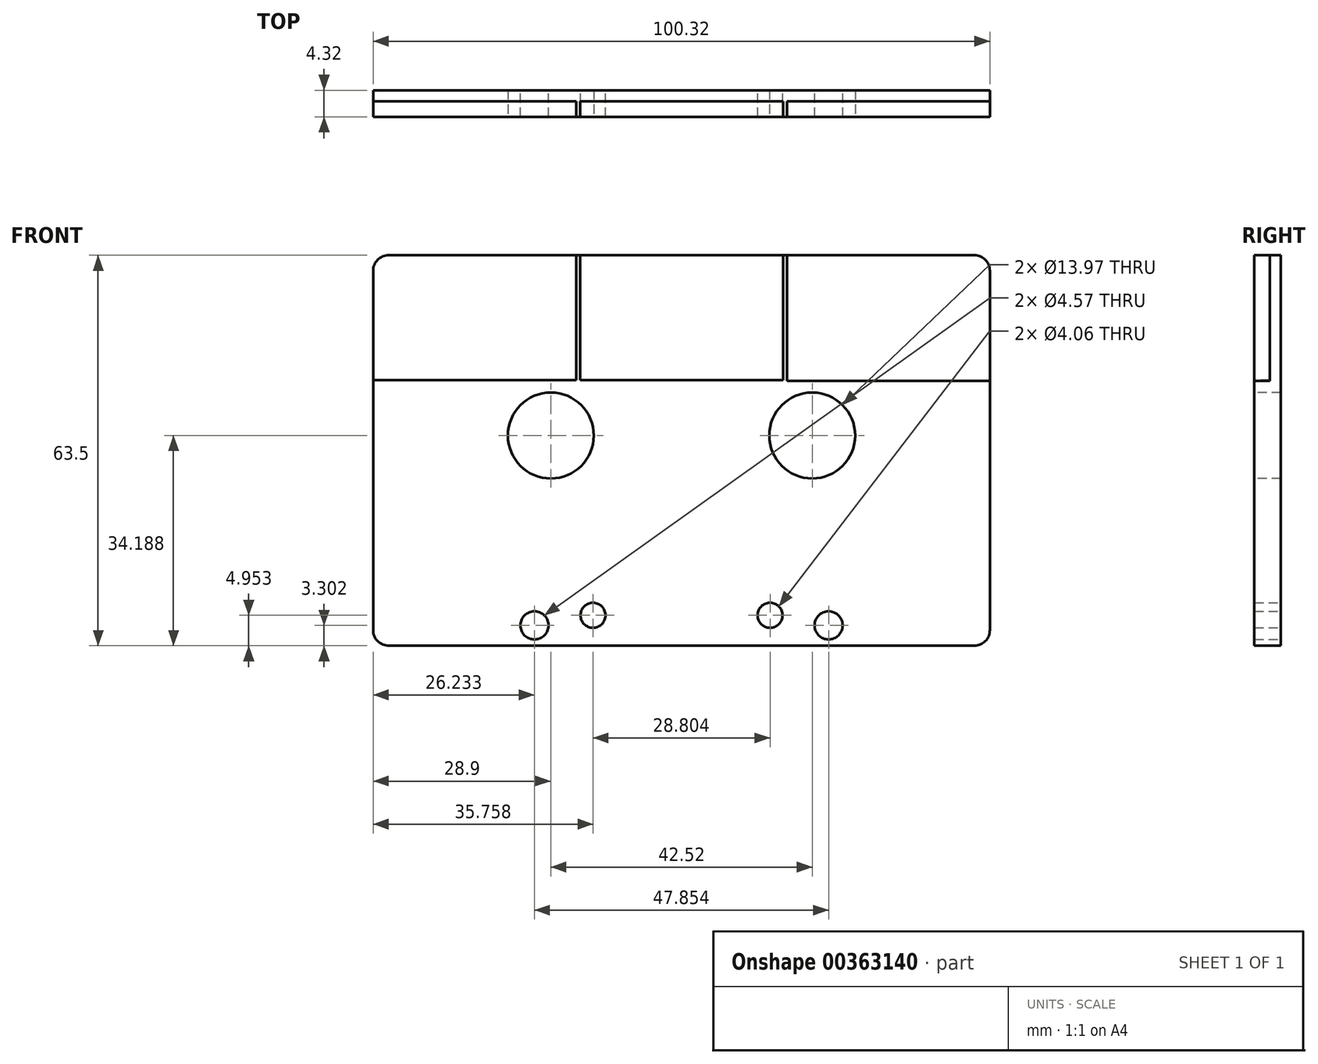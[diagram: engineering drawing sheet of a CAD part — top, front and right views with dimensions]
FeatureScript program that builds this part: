
annotation { "Feature Type Name" : "Feature", "Feature Type Description" : "" }
export const myFeature = defineFeature(function(context is Context, id is Id, definition is map)
    precondition{}
    {
        {
            var Q0;
            Q0=qCreatedBy(makeId("Front.planeOp"),FACE);
            var sketch = newSketch(context, id + "F0", { "sketchPlane" : qUnion([Q0])});
            skLineSegment(sketch, "E0.bottom", {"start": v(-47.63, 0) * mm, "end": v(47.63, 0) * mm});
            skLineSegment(sketch, "E0.top", {"start": v(-47.63, -63.5) * mm, "end": v(47.63, -63.5) * mm});
            skLineSegment(sketch, "E0.left", {"start": v(-50.17, -2.54) * mm, "end": v(-50.17, -60.96) * mm});
            skLineSegment(sketch, "E0.right", {"start": v(50.17, -2.54) * mm, "end": v(50.17, -60.96) * mm});
            skPoint(sketch, "E1.visualSharp", {"position": v(-50.17, 0) * mm});
            skArc(sketch, "E1.filletArc", {"start": v(-47.63, 0) * mm, "mid": v(-49.42, -0.74) * mm, "end": v(-50.17, -2.54) * mm});
            skPoint(sketch, "E2.visualSharp", {"position": v(50.17, 0) * mm});
            skArc(sketch, "E2.filletArc", {"start": v(50.17, -2.54) * mm, "mid": v(49.42, -0.74) * mm, "end": v(47.63, 0) * mm});
            skPoint(sketch, "E3.visualSharp", {"position": v(50.17, -63.5) * mm});
            skArc(sketch, "E3.filletArc", {"start": v(47.63, -63.5) * mm, "mid": v(49.42, -62.76) * mm, "end": v(50.17, -60.96) * mm});
            skPoint(sketch, "E4.visualSharp", {"position": v(-50.17, -63.5) * mm});
            skArc(sketch, "E4.filletArc", {"start": v(-50.16, -60.96) * mm, "mid": v(-49.42, -62.76) * mm, "end": v(-47.63, -63.5) * mm});
            skSolve(sketch);
        }
        {
            var Q0;
            Q0 = qSketchRegion(id + "F0", true);
            extrude(context, id + "F1", {"entities" : qUnion([Q0]), "depth" : 4.32 * mm});
        }
        {
            var Q0;
            Q0=makeQuery(id+"F1.opExtrude","CAP_FACE",FACE,{"disambiguationData":[OSD([sQuery(id+"F0.wireOp",EDGE,"E0.bottom"),sQuery(id+"F0.wireOp",EDGE,"E0.top"),sQuery(id+"F0.wireOp",EDGE,"E0.left"),sQuery(id+"F0.wireOp",EDGE,"E0.right"),sQuery(id+"F0.wireOp",EDGE,"E1.filletArc"),sQuery(id+"F0.wireOp",EDGE,"E2.filletArc"),sQuery(id+"F0.wireOp",EDGE,"E3.filletArc"),sQuery(id+"F0.wireOp",EDGE,"E4.filletArc")])],"isStart":false});
            var sketch = newSketch(context, id + "F2", { "sketchPlane" : qUnion([Q0])});
            skPoint(sketch, "E5", {"position": v(21.26, -29.31) * mm});
            skPoint(sketch, "E6", {"position": v(-21.26, -29.31) * mm});
            skSolve(sketch);
        }
        {
            var Q0;
            Q0=sQuery(id+"F2.wireOp",VERTEX,"E6");
            var Q1;
            Q1=sQuery(id+"F2.wireOp",VERTEX,"E5");
            var Q2;
            Q2=makeQuery(id+"F1.opExtrude","SWEPT_BODY",BODY,{"disambiguationData":[OSD([sQuery(id+"F0.wireOp",EDGE,"E0.bottom"),sQuery(id+"F0.wireOp",EDGE,"E0.top"),sQuery(id+"F0.wireOp",EDGE,"E0.left"),sQuery(id+"F0.wireOp",EDGE,"E0.right"),sQuery(id+"F0.wireOp",EDGE,"E1.filletArc"),sQuery(id+"F0.wireOp",EDGE,"E2.filletArc"),sQuery(id+"F0.wireOp",EDGE,"E3.filletArc"),sQuery(id+"F0.wireOp",EDGE,"E4.filletArc")])]});
            hole(context, id + "F3", {"style" : HoleStyle.SIMPLE, "endStyle" : HoleEndStyle.THROUGH, "holeDiameter" : 13.97 * mm, "isTappedThrough" : true, "tappedDepth" : 12.7 * mm, "tapClearance" : 3, "startFromSketch" : true, "locations" : qUnion([Q0, Q1]), "scope" : qUnion([Q2])});
        }
        {
            var Q0;
            Q0=makeQuery(id+"F1.opExtrude","CAP_FACE",FACE,{"disambiguationData":[OSD([sQuery(id+"F0.wireOp",EDGE,"E0.bottom"),sQuery(id+"F0.wireOp",EDGE,"E0.top"),sQuery(id+"F0.wireOp",EDGE,"E0.left"),sQuery(id+"F0.wireOp",EDGE,"E0.right"),sQuery(id+"F0.wireOp",EDGE,"E1.filletArc"),sQuery(id+"F0.wireOp",EDGE,"E2.filletArc"),sQuery(id+"F0.wireOp",EDGE,"E3.filletArc"),sQuery(id+"F0.wireOp",EDGE,"E4.filletArc")])],"isStart":false});
            var sketch = newSketch(context, id + "F4", { "sketchPlane" : qUnion([Q0])});
            skLineSegment(sketch, "E7.bottom", {"start": v(-16.51, 0) * mm, "end": v(16.5, 0) * mm});
            skLineSegment(sketch, "E7.top", {"start": v(-16.51, -20.32) * mm, "end": v(16.5, -20.32) * mm});
            skLineSegment(sketch, "E7.left", {"start": v(-16.51, 0) * mm, "end": v(-16.51, -20.32) * mm});
            skLineSegment(sketch, "E7.right", {"start": v(16.51, 0) * mm, "end": v(16.51, -20.32) * mm});
            skLineSegment(sketch, "E8.bottom", {"start": v(-50.17, 0) * mm, "end": v(-17.14, 0) * mm});
            skLineSegment(sketch, "E8.top", {"start": v(-50.17, -20.32) * mm, "end": v(-17.14, -20.32) * mm});
            skLineSegment(sketch, "E8.left", {"start": v(-50.17, 0) * mm, "end": v(-50.17, -20.32) * mm});
            skLineSegment(sketch, "E8.right", {"start": v(-17.14, 0) * mm, "end": v(-17.14, -20.32) * mm});
            skLineSegment(sketch, "E9.bottom", {"start": v(17.14, 0) * mm, "end": v(50.17, 0) * mm});
            skLineSegment(sketch, "E9.top", {"start": v(17.14, -20.4) * mm, "end": v(50.17, -20.4) * mm});
            skLineSegment(sketch, "E9.left", {"start": v(17.14, 0) * mm, "end": v(17.14, -20.4) * mm});
            skLineSegment(sketch, "E9.right", {"start": v(50.17, 0) * mm, "end": v(50.17, -20.4) * mm});
            skSolve(sketch);
        }
        {
            var Q0;
            Q0 = qSketchRegion(id + "F4", true);
            extrude(context, id + "F5", {"entities" : qUnion([Q0]), "operationType" : NewBodyOperationType.REMOVE, "oppositeDirection" : true, "depth" : 2.54 * mm});
        }
        {
            var Q0;
            Q0=makeQuery(id+"F1.opExtrude","CAP_FACE",FACE,{"disambiguationData":[OSD([sQuery(id+"F0.wireOp",EDGE,"E0.bottom"),sQuery(id+"F0.wireOp",EDGE,"E0.top"),sQuery(id+"F0.wireOp",EDGE,"E0.left"),sQuery(id+"F0.wireOp",EDGE,"E0.right"),sQuery(id+"F0.wireOp",EDGE,"E1.filletArc"),sQuery(id+"F0.wireOp",EDGE,"E2.filletArc"),sQuery(id+"F0.wireOp",EDGE,"E3.filletArc"),sQuery(id+"F0.wireOp",EDGE,"E4.filletArc")])],"isStart":true});
            var sketch = newSketch(context, id + "F6", { "sketchPlane" : qUnion([Q0])});
            skLineSegment(sketch, "E10", {"start": v(-34.93, -63.5) * mm, "end": v(-31.24, -47.62) * mm});
            skLineSegment(sketch, "E11", {"start": v(-31.24, -47.62) * mm, "end": v(31.24, -47.62) * mm});
            skLineSegment(sketch, "E12", {"start": v(31.24, -47.62) * mm, "end": v(34.93, -63.5) * mm});
            skLineSegment(sketch, "E13", {"start": v(34.93, -63.5) * mm, "end": v(-34.93, -63.5) * mm});
            skSolve(sketch);
        }
        {
            var Q0;
            {var subQ8=sQuery(id+"F6.wireOp",EDGE,"E10");Q0=makeQuery(id+"F6.imprint","IMPRINT",FACE,{"disambiguationData":[TD([[makeQuery(id+"F6.imprint","IMPRINT",EDGE,{"derivedFrom":subQ8}),1.0]])]});}
            var sketch = newSketch(context, id + "F7", { "sketchPlane" : qUnion([Q0])});
            skLineSegment(sketch, "E14", {"start": v(-34.7, -60.2) * mm, "end": v(34.2, -60.2) * mm, "construction": true});
            skLineSegment(sketch, "E15", {"start": v(-34.36, -58.55) * mm, "end": v(33.74, -58.55) * mm, "construction": true});
            skPoint(sketch, "E16", {"position": v(-23.93, -60.2) * mm});
            skPoint(sketch, "E17", {"position": v(23.93, -60.2) * mm});
            skPoint(sketch, "E18", {"position": v(-14.4, -58.55) * mm});
            skPoint(sketch, "E19", {"position": v(14.4, -58.55) * mm});
            skSolve(sketch);
        }
        {
            var Q0;
            Q0=sQuery(id+"F7.wireOp",VERTEX,"E16");
            var Q1;
            Q1=sQuery(id+"F7.wireOp",VERTEX,"E17");
            var Q2;
            Q2=makeQuery(id+"F1.opExtrude","SWEPT_BODY",BODY,{"disambiguationData":[OSD([sQuery(id+"F0.wireOp",EDGE,"E0.bottom"),sQuery(id+"F0.wireOp",EDGE,"E0.top"),sQuery(id+"F0.wireOp",EDGE,"E0.left"),sQuery(id+"F0.wireOp",EDGE,"E0.right"),sQuery(id+"F0.wireOp",EDGE,"E1.filletArc"),sQuery(id+"F0.wireOp",EDGE,"E2.filletArc"),sQuery(id+"F0.wireOp",EDGE,"E3.filletArc"),sQuery(id+"F0.wireOp",EDGE,"E4.filletArc")])]});
            hole(context, id + "F8", {"style" : HoleStyle.SIMPLE, "endStyle" : HoleEndStyle.THROUGH, "holeDiameter" : 4.57 * mm, "isTappedThrough" : true, "tappedDepth" : 12.7 * mm, "tapClearance" : 3, "startFromSketch" : true, "locations" : qUnion([Q0, Q1]), "scope" : qUnion([Q2])});
        }
        {
            var Q0;
            Q0=sQuery(id+"F7.wireOp",VERTEX,"E18");
            var Q1;
            Q1=sQuery(id+"F7.wireOp",VERTEX,"E19");
            var Q2;
            Q2=makeQuery(id+"F1.opExtrude","SWEPT_BODY",BODY,{"disambiguationData":[OSD([sQuery(id+"F0.wireOp",EDGE,"E0.bottom"),sQuery(id+"F0.wireOp",EDGE,"E0.top"),sQuery(id+"F0.wireOp",EDGE,"E0.left"),sQuery(id+"F0.wireOp",EDGE,"E0.right"),sQuery(id+"F0.wireOp",EDGE,"E1.filletArc"),sQuery(id+"F0.wireOp",EDGE,"E2.filletArc"),sQuery(id+"F0.wireOp",EDGE,"E3.filletArc"),sQuery(id+"F0.wireOp",EDGE,"E4.filletArc")])]});
            hole(context, id + "F9", {"style" : HoleStyle.SIMPLE, "endStyle" : HoleEndStyle.THROUGH, "holeDiameter" : 4.06 * mm, "isTappedThrough" : true, "tappedDepth" : 12.7 * mm, "tapClearance" : 3, "startFromSketch" : true, "locations" : qUnion([Q0, Q1]), "scope" : qUnion([Q2])});
        }
    });
